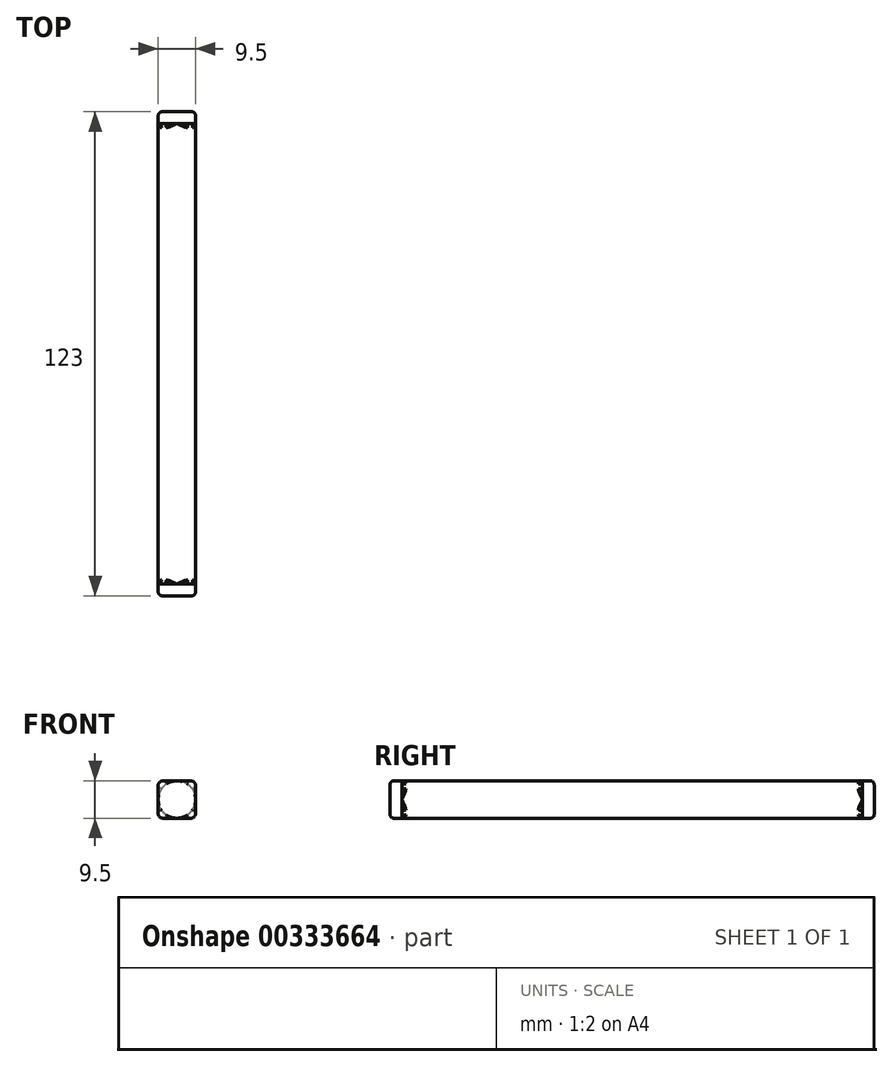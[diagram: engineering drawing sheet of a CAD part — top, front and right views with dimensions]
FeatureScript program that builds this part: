
annotation { "Feature Type Name" : "Feature", "Feature Type Description" : "" }
export const myFeature = defineFeature(function(context is Context, id is Id, definition is map)
    precondition{}
    {
        {
            var Q0;
            Q0=qCreatedBy(makeId("Front.planeOp"),FACE);
            var sketch = newSketch(context, id + "F0", { "sketchPlane" : qUnion([Q0])});
            skLineSegment(sketch, "E0.bottom", {"start": v(-3.55, 4.75) * mm, "end": v(3.55, 4.75) * mm});
            skLineSegment(sketch, "E0.top", {"start": v(-3.55, -4.75) * mm, "end": v(3.55, -4.75) * mm});
            skLineSegment(sketch, "E0.left", {"start": v(-4.75, 3.55) * mm, "end": v(-4.75, -3.55) * mm});
            skLineSegment(sketch, "E0.right", {"start": v(4.75, 3.55) * mm, "end": v(4.75, -3.55) * mm});
            skCircle(sketch, "E1", {"center": v(0, 0) * mm, "radius": 4.75 * mm});
            skPoint(sketch, "E2.visualSharp", {"position": v(-4.75, 4.75) * mm});
            skArc(sketch, "E2.filletArc", {"start": v(-3.55, 4.75) * mm, "mid": v(-4.4, 4.4) * mm, "end": v(-4.75, 3.55) * mm});
            skPoint(sketch, "E3.visualSharp", {"position": v(-4.75, -4.75) * mm});
            skArc(sketch, "E3.filletArc", {"start": v(-4.75, -3.55) * mm, "mid": v(-4.4, -4.4) * mm, "end": v(-3.55, -4.75) * mm});
            skPoint(sketch, "E4.visualSharp", {"position": v(4.75, -4.75) * mm});
            skArc(sketch, "E4.filletArc", {"start": v(3.55, -4.75) * mm, "mid": v(4.4, -4.4) * mm, "end": v(4.75, -3.55) * mm});
            skPoint(sketch, "E5.visualSharp", {"position": v(4.75, 4.75) * mm});
            skArc(sketch, "E5.filletArc", {"start": v(4.75, 3.55) * mm, "mid": v(4.4, 4.4) * mm, "end": v(3.55, 4.75) * mm});
            skSolve(sketch);
        }
        {
            var Q0;
            {var subQ0=sQuery(id+"F0.wireOp",EDGE,"E1");var subQ1=makeQuery(id+"F0.imprint","INTERSECT",VERTEX,{"derivedFrom":[sQuery(id+"F0.wireOp",EDGE,"E0.bottom"),subQ0]});Q0=makeQuery(id+"F0.imprint","IMPRINT",FACE,{"disambiguationData":[TD([[makeQuery(id+"F0.imprint","IMPRINT",EDGE,{"disambiguationData":[TD([[subQ1,1.0]])],"derivedFrom":subQ0}),1.0]])]});}
            extrude(context, id + "F1", {"entities" : qUnion([Q0]), "depth" : 120 * mm});
        }
        {
            var Q0;
            Q0 = qSketchRegion(id + "F0", true);
            extrude(context, id + "F2", {"entities" : qUnion([Q0]), "operationType" : NewBodyOperationType.ADD, "depth" : 3 * mm});
        }
        {
            var Q0;
            Q0=makeQuery(id+"F2.boolean.opBoolean","INTERSECT",EDGE,{"disambiguationData":[OD(3.0)],"derivedFrom":[makeQuery(id+"F1.opExtrude","SWEPT_FACE",FACE,{"disambiguationData":[OSD([sQuery(id+"F0.wireOp",EDGE,"E1")])]}),makeQuery(id+"F2.opExtrude","CAP_FACE",FACE,{"disambiguationData":[OSD([sQuery(id+"F0.wireOp",EDGE,"E0.bottom"),sQuery(id+"F0.wireOp",EDGE,"E0.top"),sQuery(id+"F0.wireOp",EDGE,"E0.left"),sQuery(id+"F0.wireOp",EDGE,"E0.right"),sQuery(id+"F0.wireOp",EDGE,"E2.filletArc"),sQuery(id+"F0.wireOp",EDGE,"E3.filletArc"),sQuery(id+"F0.wireOp",EDGE,"E4.filletArc"),sQuery(id+"F0.wireOp",EDGE,"E5.filletArc")])],"isStart":false})]});
            var Q1;
            Q1=makeQuery(id+"F2.boolean.opBoolean","MERGE",FACE,{"derivedFrom":[makeQuery(id+"F1.opExtrude","CAP_FACE",FACE,{"disambiguationData":[OSD([sQuery(id+"F0.wireOp",EDGE,"E1")])],"isStart":true}),makeQuery(id+"F2.opExtrude","CAP_FACE",FACE,{"disambiguationData":[OSD([sQuery(id+"F0.wireOp",EDGE,"E0.bottom"),sQuery(id+"F0.wireOp",EDGE,"E0.top"),sQuery(id+"F0.wireOp",EDGE,"E0.left"),sQuery(id+"F0.wireOp",EDGE,"E0.right"),sQuery(id+"F0.wireOp",EDGE,"E2.filletArc"),sQuery(id+"F0.wireOp",EDGE,"E3.filletArc"),sQuery(id+"F0.wireOp",EDGE,"E4.filletArc"),sQuery(id+"F0.wireOp",EDGE,"E5.filletArc")])],"isStart":true})]});
            fillet(context, id + "F3", {"entities" : qUnion([Q0, Q1]), "radius" : 1 * mm, "tangentPropagation" : true, "allowEdgeOverflow" : false});
        }
        {
            var Q0;
            Q0=makeQuery(id+"F1.opExtrude","CAP_FACE",FACE,{"disambiguationData":[OSD([sQuery(id+"F0.wireOp",EDGE,"E1")])],"isStart":false});
            var sketch = newSketch(context, id + "F4", { "sketchPlane" : qUnion([Q0])});
            skLineSegment(sketch, "E6.bottom", {"start": v(-3.55, 4.75) * mm, "end": v(3.55, 4.75) * mm});
            skLineSegment(sketch, "E6.top", {"start": v(-3.55, -4.75) * mm, "end": v(3.55, -4.75) * mm});
            skLineSegment(sketch, "E6.left", {"start": v(-4.75, 3.55) * mm, "end": v(-4.75, -3.55) * mm});
            skLineSegment(sketch, "E6.right", {"start": v(4.75, 3.55) * mm, "end": v(4.75, -3.55) * mm});
            skPoint(sketch, "E7.visualSharp", {"position": v(-4.75, 4.75) * mm});
            skArc(sketch, "E7.filletArc", {"start": v(-3.55, 4.75) * mm, "mid": v(-4.4, 4.4) * mm, "end": v(-4.75, 3.55) * mm});
            skPoint(sketch, "E8.visualSharp", {"position": v(4.75, 4.75) * mm});
            skArc(sketch, "E8.filletArc", {"start": v(4.75, 3.55) * mm, "mid": v(4.4, 4.4) * mm, "end": v(3.55, 4.75) * mm});
            skPoint(sketch, "E9.visualSharp", {"position": v(4.75, -4.75) * mm});
            skArc(sketch, "E9.filletArc", {"start": v(3.55, -4.75) * mm, "mid": v(4.4, -4.4) * mm, "end": v(4.75, -3.55) * mm});
            skPoint(sketch, "E10.visualSharp", {"position": v(-4.75, -4.75) * mm});
            skArc(sketch, "E10.filletArc", {"start": v(-4.75, -3.55) * mm, "mid": v(-4.4, -4.4) * mm, "end": v(-3.55, -4.75) * mm});
            skSolve(sketch);
        }
        {
            var Q0;
            Q0 = qSketchRegion(id + "F4", true);
            extrude(context, id + "F5", {"entities" : qUnion([Q0]), "operationType" : NewBodyOperationType.ADD, "depth" : 3 * mm});
        }
        {
            var Q0;
            {var subQ0=sQuery(id+"F0.wireOp",EDGE,"E1");var subQ1=sQuery(id+"F4.wireOp",EDGE,"E6.left");var subQ2=sQuery(id+"F4.wireOp",EDGE,"E6.bottom");Q0=makeQuery(id+"F5.boolean.opBoolean","SPLIT",EDGE,{"disambiguationData":[TD([makeQuery(id+"F1.opExtrude","SWEPT_FACE",FACE,{"disambiguationData":[OSD([subQ0])]}),makeQuery(id+"F5.opExtrude","SWEPT_FACE",FACE,{"disambiguationData":[OSD([subQ2])]}),makeQuery(id+"F5.opExtrude","CAP_FACE",FACE,{"disambiguationData":[OSD([subQ2,sQuery(id+"F4.wireOp",EDGE,"E6.top"),subQ1,sQuery(id+"F4.wireOp",EDGE,"E6.right"),sQuery(id+"F4.wireOp",EDGE,"E7.filletArc"),sQuery(id+"F4.wireOp",EDGE,"E8.filletArc"),sQuery(id+"F4.wireOp",EDGE,"E9.filletArc"),sQuery(id+"F4.wireOp",EDGE,"E10.filletArc")])],"isStart":true}),makeQuery(id+"F5.opExtrude","SWEPT_FACE",FACE,{"disambiguationData":[OSD([subQ1])]})])],"derivedFrom":makeQuery(id+"F1.opExtrude","CAP_EDGE",EDGE,{"disambiguationData":[OSD([subQ0])],"isStart":false})});}
            var Q1;
            Q1=makeQuery(id+"F1.opExtrude","SWEPT_FACE",FACE,{"disambiguationData":[OSD([sQuery(id+"F0.wireOp",EDGE,"E1")])]});
            var Q2;
            Q2=makeQuery(id+"F5.opExtrude","CAP_FACE",FACE,{"disambiguationData":[OSD([sQuery(id+"F4.wireOp",EDGE,"E6.bottom"),sQuery(id+"F4.wireOp",EDGE,"E6.top"),sQuery(id+"F4.wireOp",EDGE,"E6.left"),sQuery(id+"F4.wireOp",EDGE,"E6.right"),sQuery(id+"F4.wireOp",EDGE,"E7.filletArc"),sQuery(id+"F4.wireOp",EDGE,"E8.filletArc"),sQuery(id+"F4.wireOp",EDGE,"E9.filletArc"),sQuery(id+"F4.wireOp",EDGE,"E10.filletArc")])],"isStart":false});
            fillet(context, id + "F6", {"entities" : qUnion([Q0, Q1, Q2]), "radius" : 1 * mm, "tangentPropagation" : true, "allowEdgeOverflow" : false});
        }
    });
